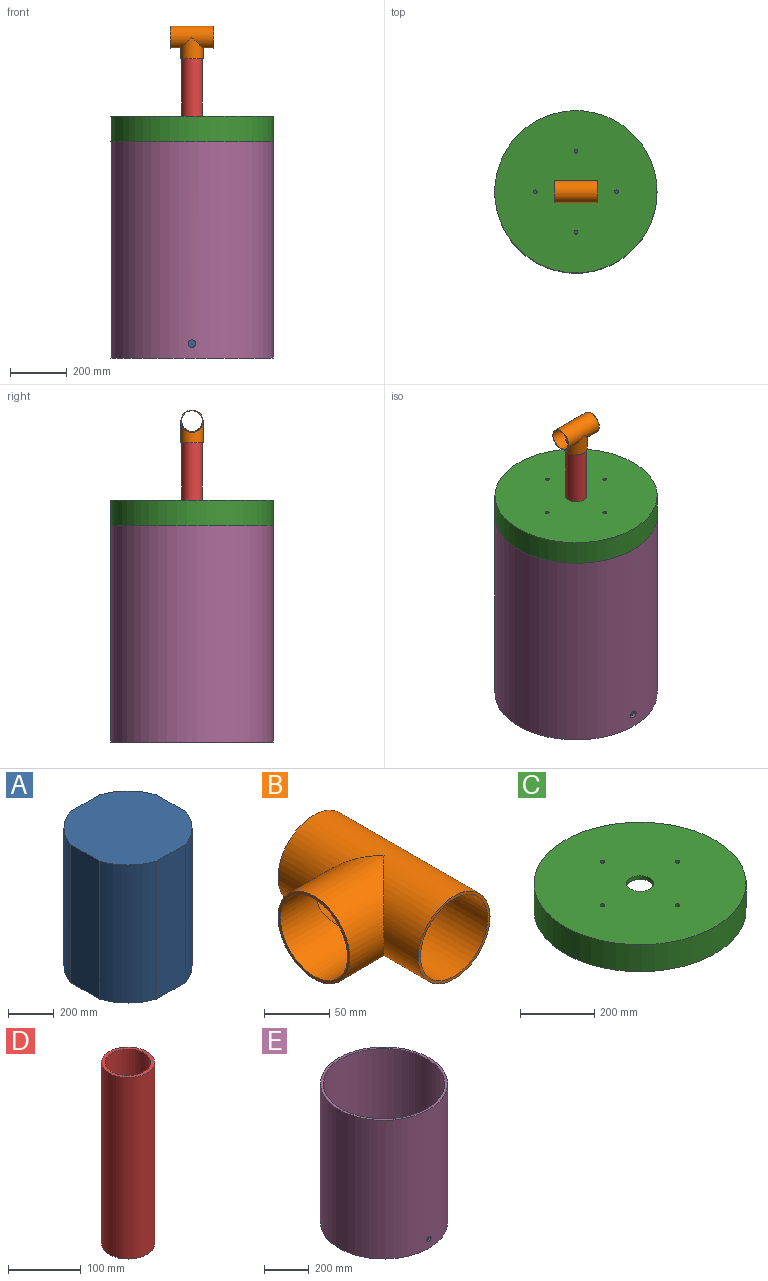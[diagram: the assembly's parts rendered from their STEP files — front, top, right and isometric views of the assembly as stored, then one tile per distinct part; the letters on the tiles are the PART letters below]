
ASSEMBLY  parts=5 mates=4
PART A: 10 faces, bbox 529.6x529.6x736.6 mm
  f0: cylinder r=279.4mm len=736.6mm, axis (0,0,-1), area 189620.6mm2, adj f4,f5,f6,f9
  f1: cylinder r=279.4mm len=736.6mm, axis (0,0,-1), area 189620.6mm2, adj f4,f5,f8,f9
  f2: cylinder r=279.4mm len=736.6mm, axis (0,0,-1), area 189620.6mm2, adj f4,f5,f7,f8
  f3: cylinder r=279.4mm len=736.6mm, axis (0,0,-1), area 189620.6mm2, adj f4,f5,f6,f7
  f4: plane 529.6x529.6mm, normal (0,0,1), area 238267.5mm2, adj f0,f1,f2,f3,f6,f7,f8,f9
  f5: plane 529.6x529.6mm, normal (0,0,-1), area 238267.5mm2, adj f0,f1,f2,f3,f6,f7,f8,f9
  f6: plane 736.6x178.28mm, normal (1,0,0), area 131322.2mm2, adj f0,f3,f4,f5
  f7: plane 736.6x178.28mm, normal (0,-1,0), area 131322.2mm2, adj f2,f3,f4,f5
  f8: plane 736.6x178.28mm, normal (-1,0,0), area 131322.2mm2, adj f1,f2,f4,f5
  f9: plane 736.6x178.28mm, normal (0,1,0), area 131322.2mm2, adj f0,f1,f4,f5
PART B: 7 faces, bbox 115.3x152.4x78.2 mm
  f0: cylinder r=36.51mm len=152.4mm, axis (0,1,0), area 29630.2mm2, adj f1,f2,f6
  f1: plane 78.18x78.18mm, normal (0,-1,0), area 612.3mm2, adj f0,f3
  f2: plane 78.18x78.18mm, normal (0,1,0), area 612.3mm2, adj f0,f3
  f3: cylinder r=39.09mm len=152.4mm, axis (0,1,0), area 31319.2mm2, adj f1,f2,f5
  f4: plane 78.18x78.18mm, normal (-1,0,0), area 612.3mm2, adj f5,f6
  f5: cylinder r=39.09mm len=78.18mm, axis (1,0,0), area 12603.5mm2, adj f3,f4
  f6: cylinder r=36.51mm len=76.2mm, axis (1,0,0), area 12148.8mm2, adj f0,f4
PART C: 10 faces, bbox 571.5x571.5x88.9 mm
  f0: cylinder r=6.35mm len=12.7mm, axis (0,0,-1), area 506.7mm2, adj f5,f8
  f1: cylinder r=6.35mm len=12.7mm, axis (0,0,-1), area 506.7mm2, adj f5,f8
  f2: cylinder r=6.35mm len=12.7mm, axis (0,0,-1), area 506.7mm2, adj f5,f8
  f3: cylinder r=6.35mm len=12.7mm, axis (0,0,-1), area 506.7mm2, adj f5,f8
  f4: cylinder r=285.75mm len=571.5mm, axis (0,0,-1), area 159612.9mm2, adj f5,f6
  f5: plane 571.5x571.5mm, normal (0,0,1), area 251825.7mm2, adj f0,f1,f2,f3,f4,f9
  f6: plane 571.5x571.5mm, normal (0,0,-1), area 22295.1mm2, adj f4,f7
  f7: cylinder r=273.05mm len=546.1mm, axis (0,0,-1), area 130730.5mm2, adj f6,f8
  f8: plane 546.1x546.1mm, normal (0,0,-1), area 229530.6mm2, adj f0,f1,f2,f3,f7,f9
  f9: cylinder r=36.51mm len=73.03mm, axis (0,0,1), area 2913.6mm2, adj f5,f8
PART D: 4 faces, bbox 73x73x304.8 mm
  f0: cylinder r=31.36mm len=304.8mm, axis (0,0,-1), area 60050.9mm2, adj f2,f3
  f1: cylinder r=36.51mm len=304.8mm, axis (0,0,-1), area 69925.6mm2, adj f2,f3
  f2: plane 73.03x73.03mm, normal (0,0,1), area 1099.4mm2, adj f0,f1
  f3: plane 73.03x73.03mm, normal (0,0,-1), area 1099.4mm2, adj f0,f1
PART E: 6 faces, bbox 571.5x571.5x762 mm
  f0: cylinder r=285.75mm len=762mm, axis (0,0,-1), area 1367549.9mm2, adj f2,f3,f5
  f1: cylinder r=273.05mm len=749.3mm, axis (0,0,-1), area 1284956.6mm2, adj f2,f4,f5
  f2: plane 571.5x571.5mm, normal (0,0,1), area 22295.1mm2, adj f0,f1
  f3: plane 571.5x571.5mm, normal (0,0,-1), area 256520.7mm2, adj f0
  f4: plane 546.1x546.1mm, normal (0,0,1), area 234225.5mm2, adj f1
  f5: cylinder r=13.33mm len=26.67mm, axis (0,1,0), area 1064.7mm2, adj f0,f1
PLACE A rot(axis=(1,0,0),180deg) t=(1591.31,362.17,1210.92)mm
PLACE B rot(axis=(-0.58,-0.58,-0.58),120deg) t=(1515.11,362.17,1591.92)mm
PLACE C t=(1591.31,362.17,1223.62)mm
PLACE D rot(axis=(0,0,-1),90deg) t=(1591.31,362.17,1210.92)mm
PLACE E t=(1591.31,362.17,461.62)mm
MATE fastened A.f0 <-> E.f0  axis (0,0,-1) through (1591.31,362.17,474.32)mm
MATE fastened D.f0 <-> A.f0  axis (0,0,-1) through (1591.31,362.17,1210.92)mm
MATE fastened D.f0 <-> B.f5  axis (0,0,-1) through (1591.31,362.17,1515.72)mm
MATE fastened E.f0 <-> C.f4  axis (0,0,1) through (1591.31,362.17,1223.62)mm
